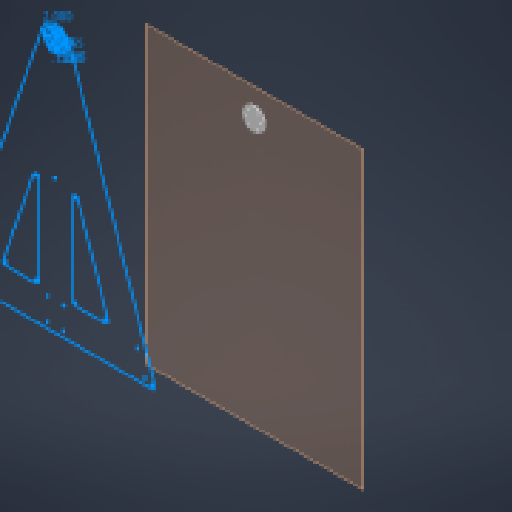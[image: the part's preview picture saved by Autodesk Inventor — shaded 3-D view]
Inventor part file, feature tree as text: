
AUTODESK INVENTOR PART (.ipt)
format: ipt  version: 2024.1 (Build 281209000, 209)  size: 386,560 bytes
history: native  units: in
note: dims shown in document units (in); Inventor stores cm internally (conversion verified against a paired STEP export)
features: extrude x8, sketch x6, other x5, projected_geometry x5, plane x2, reference x2, chamfer x1, fillet x1
ambient origin geometry x8: Origin, YZ Plane, XZ Plane, XY Plane, X Axis, Y Axis, Z Axis, Center Point
bodies: Solid1 (feature_tree)
feature tree (30):
  plane  "Work Plane1"
  sketch  "Sketch1"  dims[d0=0.1654in d1=0.1654in]
  extrude  "Extrusion1"  Depth=0.1654in
  extrude  "Extrusion2"  Depth=0.1654in
  plane  "Work Plane2"
  other  "Work Axis1"
  sketch  "Sketch2"  dims[d2=0.1654in d3=0.1654in]
  extrude  "Extrusion3"  Depth=0.1654in
  extrude  "Extrusion4"  Depth=2.0in
  extrude  "Extrusion5"  Depth=0.25in TaperAngle=0.0deg
  chamfer  "Chamfer1"  [1 undecoded]
  extrude  "Extrusion6"  Depth=0.08in
  fillet  "Fillet1"  Radius=1.0in
  sketch  "Sketch4"  dims[d6=0.002in d7=2.0in]
  extrude  "Extrusion7"  Depth=0.3425in
  extrude  "Extrusion8"  Depth=0.0625in TaperAngle=0.0deg
  reference  "Reference1"
  reference  "Reference2"
  sketch  "Sketch3"  dims[d4=0.1654in d5=0.1654in]
  projected_geometry  "Projected Loop1"
  projected_geometry  "Projected Loop2"
  sketch  "Sketch5"  dims[d8=0.125in d9=0.0in d10=0.25in d11=0.0in]
  projected_geometry  "Projected Loop3"
  sketch  "Sketch6"  dims[d12=0.002in d13=0.0in d14=0.0in d15=0.08in d16=1.0in d17=0.0in d18=0.3425in d19=0.0625in d20=0.0in d21=0.025in d22=0.125in d23=45.0deg d24=0.0625in d25=0.0in d26=0.05in d27=0.375in d28=0.0in d29=0.0in d30=0.0in d31=0.87in d32=0.0344in]
  projected_geometry  "Projected Loop4"
  projected_geometry  "Projected Loop5"
  other  "<userpath>\Documents\School\FallCAD\Trebuchet\Trebuchet.iam"
  other  "Trebuchet.iam"
  other  "FrameTop:5"
  other  "BallBearing_8x22x7mm:10"
note: 1 required parameter value undecoded (feature->parameter linkage not recoverable at this tier; creation-order binding heuristic only, values carry confidence <= 0.55)
